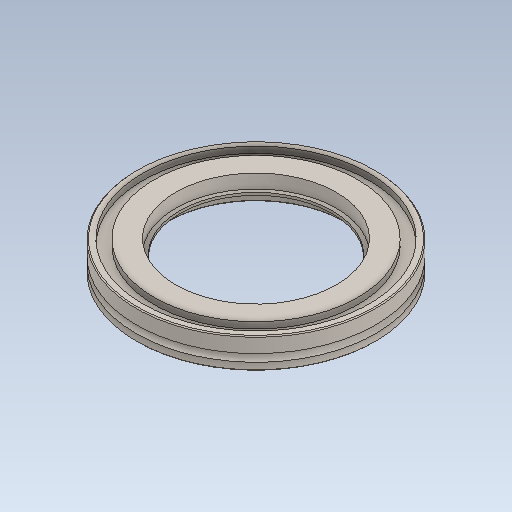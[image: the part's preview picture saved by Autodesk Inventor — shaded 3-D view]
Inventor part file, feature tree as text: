
AUTODESK INVENTOR PART (.ipt)
format: ipt  version: 2021 (Build 250183000, 183)  size: 186,368 bytes
history: native  units: in
note: dims shown in document units (in); Inventor stores cm internally (conversion verified against a paired STEP export)
features: chamfer x1
ambient origin geometry x8: Origin, YZ Plane, XZ Plane, XY Plane, X Axis, Y Axis, Z Axis, Center Point
bodies: Solid1 (feature_tree)
feature tree (1):
  chamfer  "Chamfer2"  [1 undecoded]
note: 1 required parameter value undecoded (feature->parameter linkage not recoverable at this tier; creation-order binding heuristic only, values carry confidence <= 0.55)
